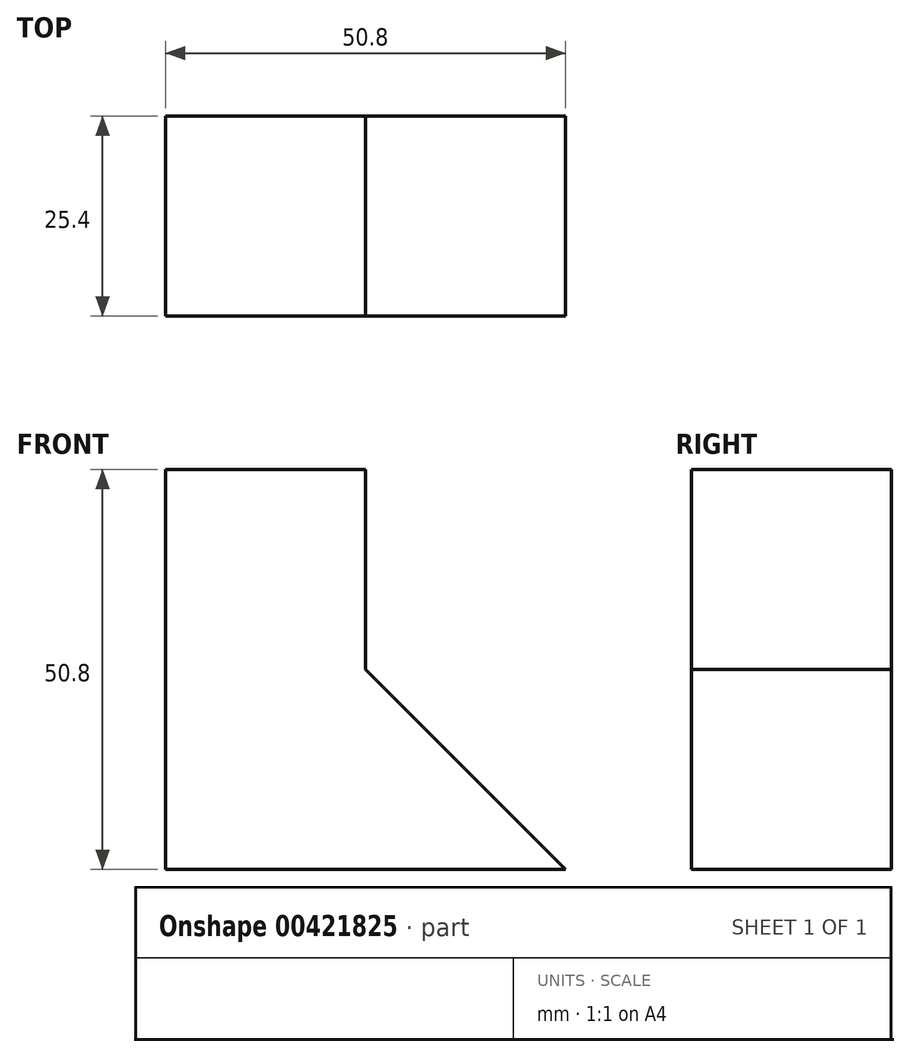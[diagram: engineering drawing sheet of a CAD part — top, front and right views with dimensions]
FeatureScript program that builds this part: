
annotation { "Feature Type Name" : "Feature", "Feature Type Description" : "" }
export const myFeature = defineFeature(function(context is Context, id is Id, definition is map)
    precondition{}
    {
        {
            var Q0;
            Q0=qCreatedBy(makeId("Front.planeOp"),FACE);
            var sketch = newSketch(context, id + "F0", { "sketchPlane" : qUnion([Q0])});
            skLineSegment(sketch, "E0", {"start": v(0, 0) * mm, "end": v(-50.8, 0) * mm});
            skLineSegment(sketch, "E1", {"start": v(-50.8, 0) * mm, "end": v(-50.8, 50.8) * mm});
            skLineSegment(sketch, "E2", {"start": v(-50.8, 50.8) * mm, "end": v(-25.4, 50.8) * mm});
            skLineSegment(sketch, "E3", {"start": v(-25.4, 50.8) * mm, "end": v(-25.4, 25.4) * mm});
            skLineSegment(sketch, "E4", {"start": v(-25.4, 25.4) * mm, "end": v(0, 0) * mm});
            skSolve(sketch);
        }
        {
            var Q0;
            Q0 = qSketchRegion(id + "F0", true);
            extrude(context, id + "F1", {"entities" : qUnion([Q0]), "depth" : 25.4 * mm});
        }
    });
